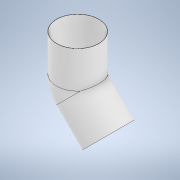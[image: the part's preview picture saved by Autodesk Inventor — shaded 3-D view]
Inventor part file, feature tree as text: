
AUTODESK INVENTOR PART (.ipt)
format: ipt  version: 2021 (Build 250183000, 183)  size: 135,168 bytes
history: native  units: mm
features: sketch x2, plane x1, sweep x1
ambient origin geometry x8: Origin, YZ Plane, XZ Plane, XY Plane, X Axis, Y Axis, Z Axis, Center Point
bodies: Solid1 (feature_tree)
feature tree (4):
  sketch  "Sketch1"  dims[d0=40.0mm d1=40.0mm]
  plane  "Work Plane1"
  sweep  "Sweep1"
  sketch  "Sketch2"  dims[d2=135.0deg d3=15.0mm d4=38.5mm d5=39.0mm d6=0.0mm d7=0.0mm]
